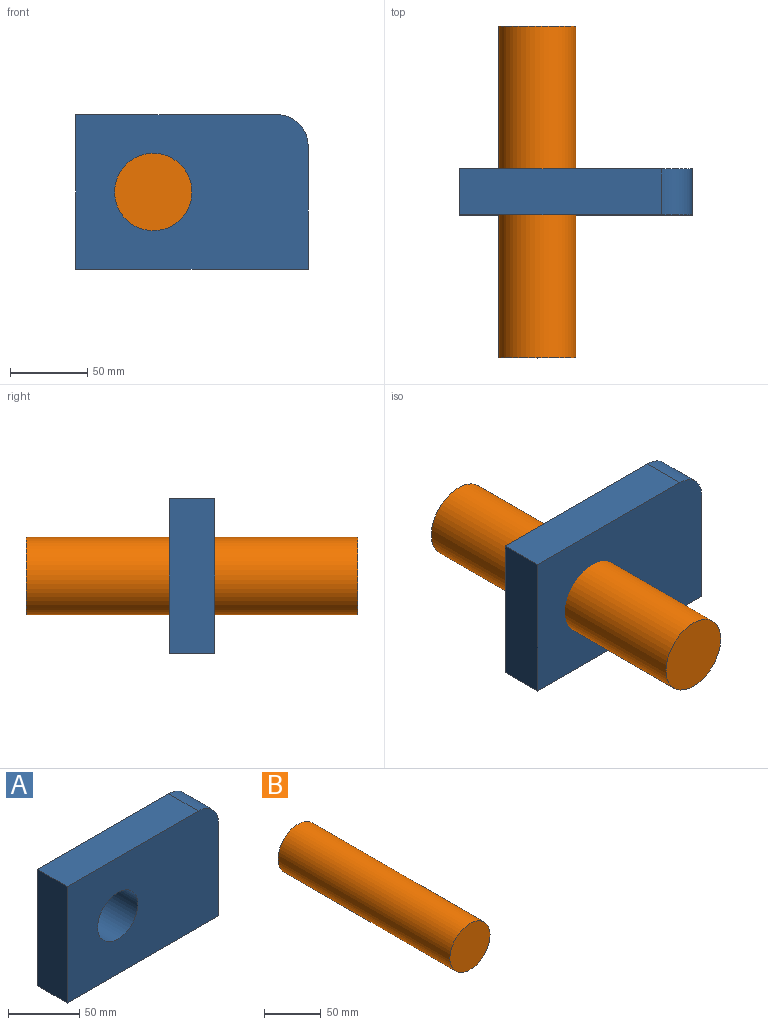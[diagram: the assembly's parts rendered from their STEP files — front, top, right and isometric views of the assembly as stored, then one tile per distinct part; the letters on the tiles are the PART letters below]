
ASSEMBLY  parts=2 mates=1
PART A: 8 faces, bbox 150x29.7x100 mm
  f0: plane 80x29.68mm, normal (1,0,0), area 2374.1mm2, adj f3,f4,f5,f7
  f1: plane 130x29.68mm, normal (0,0,1), area 3857.9mm2, adj f2,f4,f5,f7
  f2: plane 100x29.68mm, normal (-1,0,0), area 2967.7mm2, adj f1,f3,f4,f5
  f3: plane 150x29.68mm, normal (0,0,-1), area 4451.5mm2, adj f0,f2,f4,f5
  f4: plane 150x100mm, normal (0,-1,0), area 13657.5mm2, adj f0,f1,f2,f3,f6,f7
  f5: plane 150x100mm, normal (0,1,0), area 13657.5mm2, adj f0,f1,f2,f3,f6,f7
  f6: cylinder r=20mm len=40mm, axis (0,-1,0), area 3729.3mm2, adj f4,f5
  f7: cylinder r=20mm len=29.68mm, axis (0,-1,0), area 932.3mm2, adj f0,f1,f4,f5
PART B: 3 faces, bbox 50x214.4x50 mm
  f0: cylinder r=25mm len=214.39mm, axis (0,1,0), area 33676.9mm2, adj f1,f2
  f1: plane 50x50mm, normal (0,-1,0), area 1963.5mm2, adj f0
  f2: plane 50x50mm, normal (0,1,0), area 1963.5mm2, adj f0
PLACE A t=(25,-92.36,0)mm
PLACE B at identity
MATE slider A.f6 <-> B.f0  axis (0,-1,0) through (0,-107.2,0)mm
